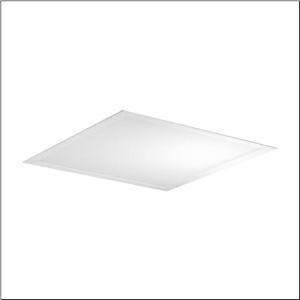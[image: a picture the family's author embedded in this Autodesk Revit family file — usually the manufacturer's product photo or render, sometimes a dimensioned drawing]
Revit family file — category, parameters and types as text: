
# Revit family: apollon_r__31_square_51mp11wd2442_8a23
name_source: partatom
category: Lighting Fixtures
units: mm (PartAtom-declared; Revit-internal decimal feet)

## family parameters
Cut with Voids When Loaded = No
Host = Face
Light Source = No
Part Type = Normal
Room Calculation Point = No
Round Connector Dimension = Use Diameter
Shared = No

## types (1)
- Apollon® 31 square (1 x LED, 4000 lm, 27.5 W, 4000K)
    Apparent Load = 28 VA
    CIE Flux Codes = 61 87 97 100 100
    Color Rendering = 80
    Color Temperature = 4000K
    Default Elevation = 1800 mm
    Description = Apollon® 31 square, office luminaire, primary optical cover: micro prismatic cover, of PMMA, CAT 2 (L<= 3000cd/m²), light emission: direct distribution, primary light characteristic: symmetric, installation type: lay-in mounting, LED, rated luminous flux: 4.000lm, luminous efficacy: 145lm/W, light colour: 840, colour temperature: 4000K, with terminal, 5-pole, mains connection: 220..240V, AC/DC, 0/50..60Hz, rated input power: 28W, housing, of aluminium, traffic white (RAL 9016), module: M625, length: 620mm, width: 620mm, height: 32mm, housing upper side, of sheet steel, galvanised, protection rating (complete): IP20, protection rating (on room side): IP40, insulation class (complete): insulation class II (safety insulation), certification: CE, ENEC, impact resistance: IK03, permissible operating ambient temperature: -20..+40°C, permissible storage temperature: -20..+60°C, packaging unit: 1 piece
    Height = 0 mm  [stored 0 ft]
    Lamp = 1 x LED
    Lamp Light Flux = 4000 lm
    Lamp Power = 27.5 W
    Lamp count = 1
    Length = 620 mm
    Luminous efficacy = 145 lm/W
    Manufacturer = Siteco
    ModVariant = No
    Model = 51MP11WD2442
    Mounting Place = Ceiling
    Mounting Type = Recessed
    Number of Poles = 1
    OnlyDefault = Yes
    Power Factor = 1
    Product Name = Apollon® 31 square
    Product group = office luminaire | ceiling recessed
    ProductGroupID = 400
    Protection Class = Protection class II
    Protection Degree = IP 20
    RLX_Detail_Level = 1
    RLX_Emergency_Light_Flux = 0 lm
    RLX_Emergency_Type = 0
    RLX_Emergency_Type_DB = No
    RlxData = <blob elided: 12941 chars, md5=2f4620a2>
    Socket = socket
    Standby Power = 0 W
    System Light Flux = 4000 lm
    System Power = 28 W
    Type Comments = Product without accessories
    Type Image = l_1291039.jpg
    URL = http://relux.com
    VarID = ---
    Voltage = 0 V
    Weight = 0.00 kg
    Width = 620 mm

note: [stored X ft] marks values corroborated as IEEE doubles in the binary element streams (Revit-internal decimal feet)

## geometry (parser evidence)
native form markers: Sweep x11
no freeform markers — native parametric forms only
